# Revit family: 402_SAV-_-_-1AC-0-0-SAV-FC-_-A
name_source: partatom
category: Mechanical Equipment
revit_build: Autodesk Revit 2018 (Build: 20170223_1515(x64)
units: mm (PartAtom-declared; Revit-internal decimal feet)

## family parameters
Always vertical = Yes
Cut with Voids When Loaded = No
Part Type = Normal
Room Calculation Point = No
Round Connector Dimension = Use Diameter
Shared = No
Work Plane-Based = No

## types (8) — shared parameters
CAT0 = Yes
CY = 256 mm
CY1 = 94 mm
Description = Savana unit, Standard, RAL 9010
Manufacturer = 2VV
P1 = 80 mm  [stored 0.262467 ft]
P2 = 5 mm  [stored 0.0164042 ft]
QmdConnectorList = 381;DP;382;DP
URL = www.2vv.cz
YP = 88 mm
magiPartTypeId = 402
magiProductFamilyId = SAV-*-*-1AC-0-0-SAV-FC-*-A

## per-type parameters (varying)
| type | CenSd_R1_6 | H | H2 | H__ve | I | R | R1 | XP | ZP | magiProductId |
| SAV-1-2R-1AC-0-0-SAV-FC-1-A-0-0 | 11 mm | 455 mm  [stored 1.49278 ft] | 228 mm | -455 mm  [stored -1.49278 ft] | 305 mm | 10 mm  [stored 0.0328084 ft] | 13 mm | 313 mm | 182 mm  [stored 0.597113 ft] | SAV-1-2R-1AC-0-0-SAV-FC-1-A |
| SAV-6-3R-1AC-0-0-SAV-FC-6-A-0-0 | 16 mm | 855 mm | 428 mm | -855 mm | 573 mm | 16 mm | 19 mm | 513 mm | 342 mm | SAV-6-3R-1AC-0-0-SAV-FC-6-A |
| SAV-4-3R-1AC-0-0-SAV-FC-4-A-0-0 | 13 mm | 755 mm | 378 mm | -755 mm | 506 mm | 13 mm | 15 mm  [stored 0.0492126 ft] | 463 mm | 302 mm | SAV-4-3R-1AC-0-0-SAV-FC-4-A |
| SAV-2-3R-1AC-0-0-SAV-FC-2-A-0-0 | 11 mm | 555 mm | 278 mm | -555 mm | 372 mm | 10 mm  [stored 0.0328084 ft] | 13 mm | 363 mm | 222 mm | SAV-2-3R-1AC-0-0-SAV-FC-2-A |
| SAV-1-3R-1AC-0-0-SAV-FC-1-A-0-0 | 11 mm | 455 mm  [stored 1.49278 ft] | 228 mm | -455 mm  [stored -1.49278 ft] | 305 mm | 10 mm  [stored 0.0328084 ft] | 13 mm | 313 mm | 182 mm  [stored 0.597113 ft] | SAV-1-3R-1AC-0-0-SAV-FC-1-A |
| SAV-6-2R-1AC-0-0-SAV-FC-6-A-0-0 | 13 mm | 855 mm | 428 mm | -855 mm | 573 mm | 13 mm | 15 mm  [stored 0.0492126 ft] | 513 mm | 342 mm | SAV-6-2R-1AC-0-0-SAV-FC-6-A |
| SAV-4-2R-1AC-0-0-SAV-FC-4-A-0-0 | 11 mm | 755 mm | 378 mm | -755 mm | 506 mm | 10 mm  [stored 0.0328084 ft] | 13 mm | 463 mm | 302 mm | SAV-4-2R-1AC-0-0-SAV-FC-4-A |
| SAV-2-2R-1AC-0-0-SAV-FC-2-A-0-0 | 11 mm | 555 mm | 278 mm | -555 mm | 372 mm | 10 mm  [stored 0.0328084 ft] | 13 mm | 363 mm | 222 mm | SAV-2-2R-1AC-0-0-SAV-FC-2-A |

note: column(s) folded — value = type name in every type: MC Product Code

note: [stored X ft] marks values corroborated as IEEE doubles in the binary element streams (Revit-internal decimal feet)

## geometry (parser evidence)
native form markers: Blend x4, Sweep x2
no freeform markers — native parametric forms only
